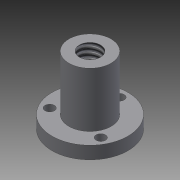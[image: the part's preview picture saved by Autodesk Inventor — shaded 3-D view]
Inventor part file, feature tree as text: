
AUTODESK INVENTOR PART (.ipt)
format: ipt  version: 2015 (Build 190159000, 159)  size: 103,936 bytes
history: native  units: in
note: dims shown in document units (in); Inventor stores cm internally (conversion verified against a paired STEP export)
features: hole x2, sketch x2, revolve x1
ambient origin geometry x8: Origin, YZ Plane, XZ Plane, XY Plane, X Axis, Y Axis, Z Axis, Center Point
bodies: Solid1 (feature_tree)
feature tree (5):
  revolve  "Revolution1"  [1 undecoded]
  hole  "Hole1"  [1 undecoded]
  hole  "Hole2"  [1 undecoded]
  sketch  "Sketch1"  dims[d0=1.0in d1=0.188in]
  sketch  "Sketch2"  dims[d2=0.3125in d3=0.5625in d4=90.0deg d14=1.0in d15=1.0in d7=0.315in d8=1.0in d9=0.375in d10=0.25in d11=0.5635in d12=1.259in d13=0.8108in d16=120.0deg d17=120.0deg d18=0.875in d19=0.14in d20=1.0in d21=0.375in d22=0.25in d23=0.5635in d24=1.259in d25=0.8108in]
note: 3 required parameter values undecoded (feature->parameter linkage not recoverable at this tier; creation-order binding heuristic only, values carry confidence <= 0.55)